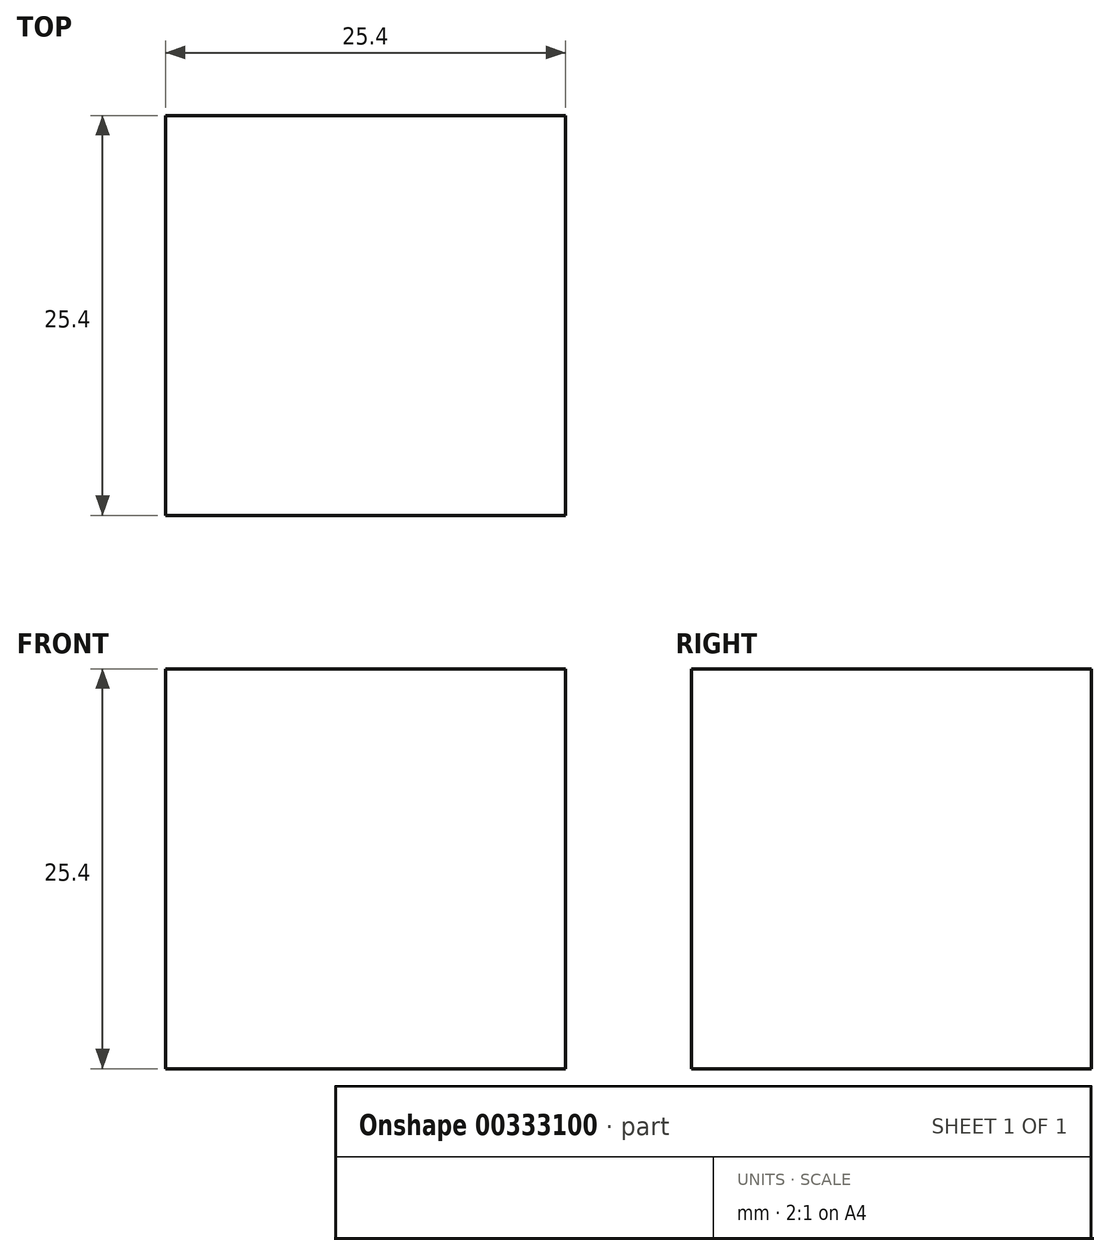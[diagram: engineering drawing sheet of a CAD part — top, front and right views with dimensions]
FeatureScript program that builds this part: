
annotation { "Feature Type Name" : "Feature", "Feature Type Description" : "" }
export const myFeature = defineFeature(function(context is Context, id is Id, definition is map)
    precondition{}
    {
        {
            var Q0;
            Q0=qCreatedBy(makeId("Top.planeOp"),FACE);
            var sketch = newSketch(context, id + "F0", { "sketchPlane" : qUnion([Q0])});
            skLineSegment(sketch, "E0.bottom", {"start": v(12.7, 12.7) * mm, "end": v(-12.7, 12.7) * mm});
            skLineSegment(sketch, "E0.top", {"start": v(12.7, -12.7) * mm, "end": v(-12.7, -12.7) * mm});
            skLineSegment(sketch, "E0.left", {"start": v(12.7, 12.7) * mm, "end": v(12.7, -12.7) * mm});
            skLineSegment(sketch, "E0.right", {"start": v(-12.7, 12.7) * mm, "end": v(-12.7, -12.7) * mm});
            skPoint(sketch, "E0.middle", {"position": v(0, 0) * mm});
            skSolve(sketch);
        }
        {
            var Q0;
            Q0=qSketchRegion(id+"F0",true);
            extrude(context, id + "F1", {"entities" : qUnion([Q0]), "depth" : 25.4 * mm});
        }
    });
